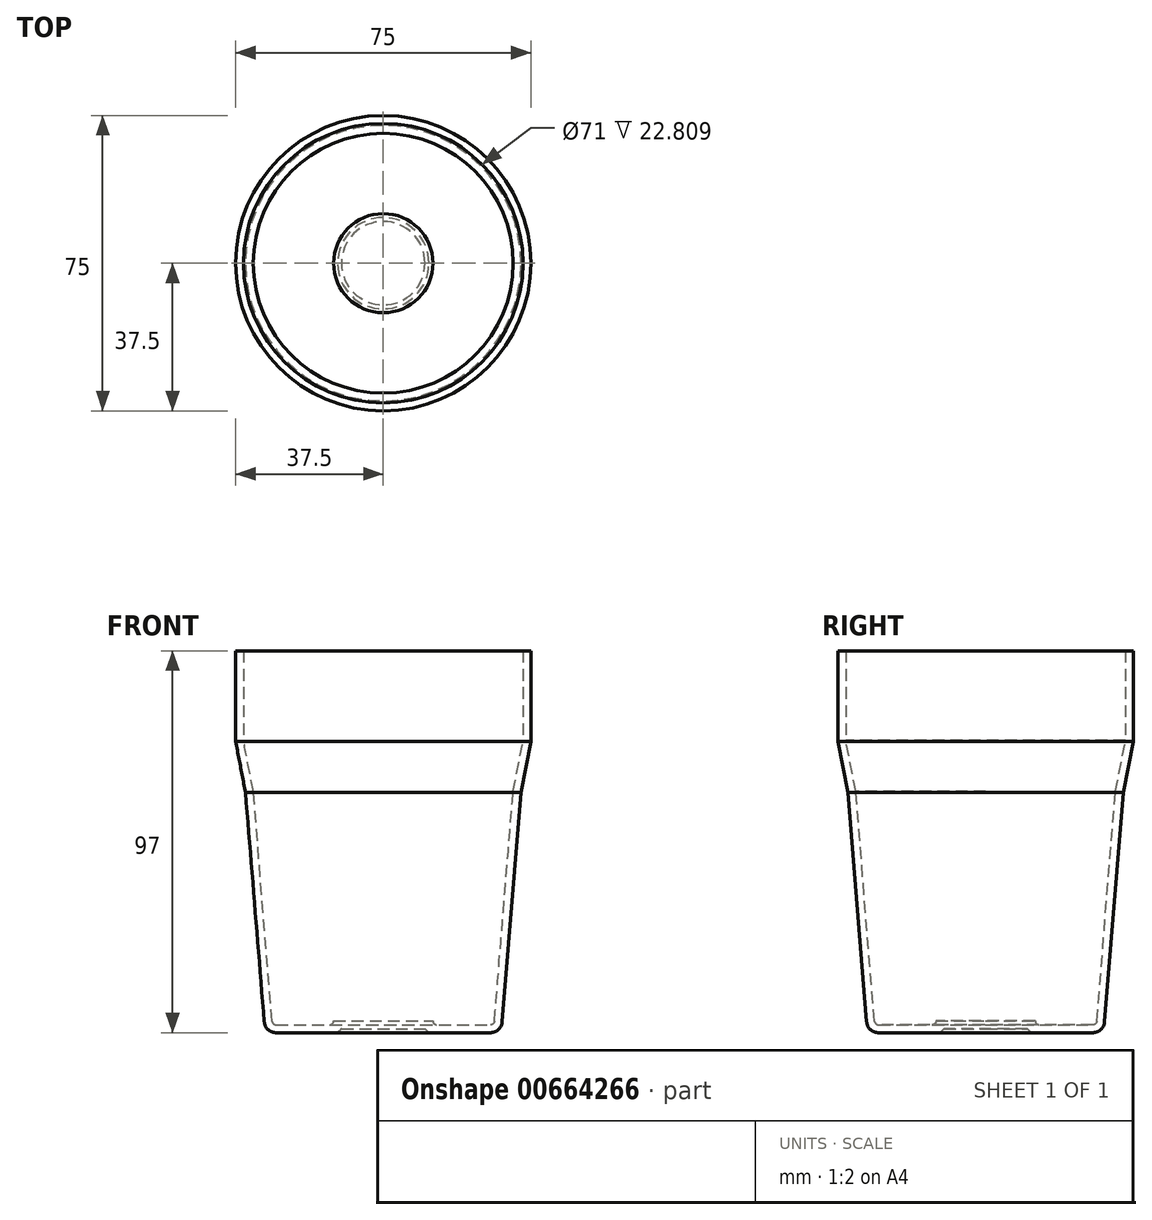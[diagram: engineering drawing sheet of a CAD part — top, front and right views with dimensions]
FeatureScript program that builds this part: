
annotation { "Feature Type Name" : "Feature", "Feature Type Description" : "" }
export const myFeature = defineFeature(function(context is Context, id is Id, definition is map)
    precondition{}
    {
        {
            var Q0;
            Q0=qCreatedBy(makeId("Front.planeOp"),FACE);
            var sketch = newSketch(context, id + "F0", { "sketchPlane" : qUnion([Q0])});
            skLineSegment(sketch, "E0", {"start": v(0, 0) * mm, "end": v(10.6, 0) * mm});
            skLineSegment(sketch, "E1", {"start": v(10.6, 0) * mm, "end": v(10.6, -1) * mm});
            skLineSegment(sketch, "E2", {"start": v(10.6, -1) * mm, "end": v(30, -1) * mm});
            skLineSegment(sketch, "E3", {"start": v(30, -1) * mm, "end": v(35, 60) * mm});
            skLineSegment(sketch, "E4", {"start": v(35, 60) * mm, "end": v(37.5, 73) * mm});
            skLineSegment(sketch, "E5", {"start": v(37.5, 73) * mm, "end": v(37.5, 96) * mm});
            skLineSegment(sketch, "E6.0", {"start": v(35.5, 73.2) * mm, "end": v(35.5, 96) * mm});
            skLineSegment(sketch, "E6.1", {"start": v(33.02, 60.27) * mm, "end": v(35.5, 73.2) * mm});
            skLineSegment(sketch, "E6.2", {"start": v(0, 2) * mm, "end": v(12.6, 2) * mm});
            skLineSegment(sketch, "E6.3", {"start": v(12.6, 2) * mm, "end": v(12.6, 1) * mm});
            skLineSegment(sketch, "E6.4", {"start": v(12.6, 1) * mm, "end": v(28.16, 1) * mm});
            skLineSegment(sketch, "E6.5", {"start": v(28.16, 1) * mm, "end": v(33.02, 60.27) * mm});
            skLineSegment(sketch, "E7", {"start": v(37.5, 96) * mm, "end": v(35.5, 96) * mm});
            skLineSegment(sketch, "E8", {"start": v(0, 2) * mm, "end": v(0, 0) * mm});
            skLineSegment(sketch, "E9", {"start": v(0, 2) * mm, "end": v(0, 96) * mm, "construction": true});
            skSolve(sketch);
        }
        {
            var Q0;
            Q0 = qSketchRegion(id + "F0", true);
            var Q1;
            Q1=sQuery(id+"F0.wireOp",EDGE,"E9");
            revolve(context, id + "F1", {"entities" : qUnion([Q0]), "axis" : qUnion([Q1]), "revolveType" : RevolveType.FULL});
        }
        {
            var Q0;
            Q0=makeQuery(id+"F1.opRevolve","SWEPT_EDGE",EDGE,{"disambiguationData":[OSD([sQuery(id+"F0.wireOp",EDGE,"E1"),sQuery(id+"F0.wireOp",EDGE,"E2")])]});
            chamfer(context, id + "F2", {"entities" : qUnion([Q0]), "width" : 1 * mm, "tangentPropagation" : true});
        }
        {
            var Q0;
            Q0=makeQuery(id+"F1.opRevolve","SWEPT_EDGE",EDGE,{"disambiguationData":[OSD([sQuery(id+"F0.wireOp",EDGE,"E2"),sQuery(id+"F0.wireOp",EDGE,"E3")])]});
            fillet(context, id + "F3", {"entities" : qUnion([Q0]), "radius" : 3 * mm, "tangentPropagation" : true, "allowEdgeOverflow" : false});
        }
        {
            var Q0;
            Q0=makeQuery(id+"F1.opRevolve","SWEPT_EDGE",EDGE,{"disambiguationData":[OSD([sQuery(id+"F0.wireOp",EDGE,"E6.4"),sQuery(id+"F0.wireOp",EDGE,"E6.5")])]});
            fillet(context, id + "F4", {"entities" : qUnion([Q0]), "radius" : 1 * mm, "tangentPropagation" : true, "allowEdgeOverflow" : false});
        }
        {
            var Q0;
            Q0=makeQuery(id+"F1.opRevolve","SWEPT_EDGE",EDGE,{"disambiguationData":[OSD([sQuery(id+"F0.wireOp",EDGE,"E6.3"),sQuery(id+"F0.wireOp",EDGE,"E6.4")])]});
            fillet(context, id + "F5", {"entities" : qUnion([Q0]), "radius" : 1 * mm, "tangentPropagation" : true, "allowEdgeOverflow" : false});
        }
    });
